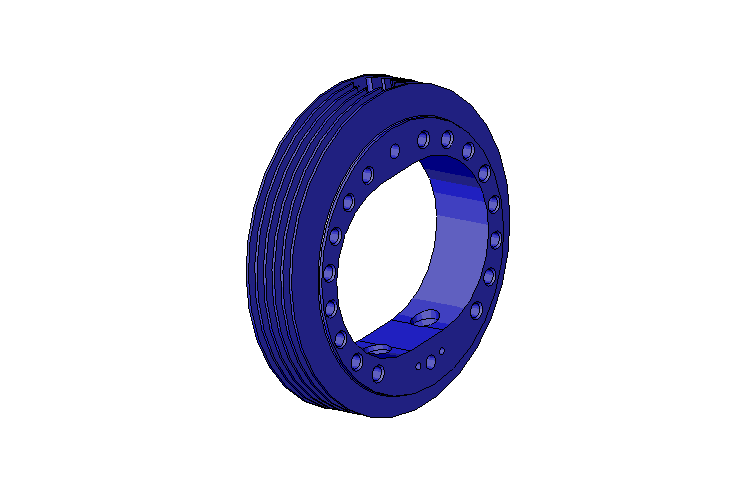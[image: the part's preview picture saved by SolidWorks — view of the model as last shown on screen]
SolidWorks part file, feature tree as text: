
SOLIDWORKS PART (.sldprt)
format: sldprt  version: not decoded by parser v0  size: 1,220,096 bytes
history: native  units: mm
features: sketch x7, cut_extrude x6, fillet x4, chamfer x3, plane x2, material x1, cut_revolve x1 + 6 further entries (+12 scaffold rows collapsed)
feature tree (42):
  scaffold x12  (default folders/planes/origin — collapsed)
  material  "Material <not specified>"
  "1.zylinder_fin<3>@1.zylinder_combined-"
  "1.zylinder_fin<1>@1.zylinder_combined-"
  "1.zylinder_fin<2>@1.zylinder_combined-"
  "1.zylinder_fin<5>@1.zylinder_combined-"
  "1.zylinder_fin<6>@1.zylinder_combined-"
  "1.zylinder_base<1>@1.zylinder_combined-"
  sketch  "Sketch2"  dims[c1.D2=49.2mm c1.D4=49.2mm c1.D17=4.0mm c1.D13=4.0mm c1.D1=6.9mm c1.D3=6.9mm c1.D5=13.8mm c1.D6=13.8mm c2.D5=6.9mm c2.D6=6.9mm c2.D7=31.0mm c2.D8=31.0mm c2.D9=30.0mm c2.D10=30.0mm c2.D11=4.5mm c3.D10=30.0mm c3.D9=4.5mm c3.D12=30.0mm c3.D13=~27.010985mm c4.D13=~162.410467deg c5.D13=~29.092008mm c6.D13=~166.293086deg c7.D13=30.0mm c8.D13=~159.137743deg c9.D13=~35.555547mm c10.D13=19.0deg c10.D14=~42.317455mm c11.D14=~146.816918deg c12.D14=~42.317455mm c13.D14=19.0deg c13.D15=~125.826232deg c14.D15=~38.234035mm c15.D15=19.0deg c15.D16=~38.234035mm c16.D16=19.0deg c16.D13=19.0deg c16.D14=19.0deg c16.D15=19.0deg]
  sketch  "Sketch3"
  cut_extrude  "Cut-Extrude2"  Depth=18mm
  plane  "Plane1"  Offset=1.5mm
  sketch  "Sketch5"  dims[D4=8.0mm D5=8.0mm D6=11.0mm D7=11.0mm D1=9.0mm D2=10.25mm D3=10.25mm]
  sketch  "Sketch9"  dims[c1.D1=6.0mm c1.D2=9.0mm c1.D3=1.6mm c1.D4=3.6mm c1.D5=0.7mm c2.D3=0.8mm c2.D4=0.9mm c2.D5=3.6mm c3.D4=0.8mm c3.D5=1.8mm c3.D6=1.8mm c3.D1=6.0mm c3.D2=9.0mm c3.D3=0.8mm c4.D4=0.8mm c4.D5=1.8mm c4.D6=1.8mm]
  plane  "Plane2"
  sketch  "Sketch11"  dims[c1.D1=6.0mm c1.D2=5.5mm c1.D3=5.5mm c2.D2=11.0mm c2.D3=6.35mm c3.D2=11.0mm c3.D3=6.35mm c3.D1=6.0mm c3.D4=4.0mm c3.D5=6.0mm c3.D6=1.6mm c3.D7=5.5mm c3.D8=7.0mm c3.D9=1.25mm c4.D2=5.5mm c4.D3=3.175mm c4.D6=0.8mm c4.D8=7.25mm c4.D9=3.5mm c5.D3=3.175mm c5.D5=~9.407712mm c6.D5=45.0deg c6.D7=~3.358757mm c7.D7=45.0deg c7.D8=6.0mm]
  cut_revolve  "Cut-Revolve1"  Angle=360deg
  cut_extrude  "Cut-Extrude5"  [1 undecoded]
  cut_extrude  "Cut-Extrude6"  [1 undecoded]
  sketch  "Sketch12"  dims[c1.D3=4.0mm c1.D4=4.0mm c1.D9=2.0mm c1.D10=2.0mm c1.D11=4.0mm c1.D1=31.0mm c1.D2=31.0mm c1.D5=5.0mm c1.D6=5.0mm c1.D7=30.0mm c1.D8=30.0mm c2.D10=~11.265744mm c2.D11=~60.827625mm]
  cut_extrude  "Cut-Extrude8"  Depth=20mm
  cut_extrude  "Cut-Extrude9"  [1 undecoded]
  sketch  "Sketch5<3>"  dims[D1=20.0mm]
  cut_extrude  "Cut-Extrude10"  Depth=20mm
  chamfer  "Chamfer1"  Distance=0.5mm Angle=45deg
  chamfer  "Chamfer2"  Distance=0.5mm Angle=45deg
  chamfer  "Chamfer3"  Distance=0.5mm Angle=45deg
  fillet  "Fillet1"  Radius=0.3mm
  fillet  "Fillet2"  Radius=0.3mm
  fillet  "Fillet3"  Radius=0.3mm
  fillet  "Fillet4"  Radius=0.3mm
decode coverage: 17 of 21 modeling features carry decoded parameters; 6 rows unclassified (native names shown)
note: ~ marks probable driven/reference dimensions
note: 3 parameter values undecoded
summary: no parameter record found for 3 features
note: suppression state not decoded; provenance and decode notes live in map.json
